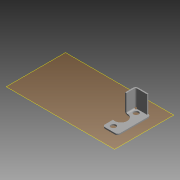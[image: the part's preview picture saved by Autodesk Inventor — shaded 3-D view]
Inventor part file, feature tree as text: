
AUTODESK INVENTOR PART (.ipt)
format: ipt  version: 2015 (Build 190159000, 159)  size: 176,640 bytes
history: native  units: mm
features: sheet_metal_op x10, sketch x4, other x4, reference x3, plane x1, hole x1
ambient origin geometry x8: Origin, YZ Plane, XZ Plane, XY Plane, X Axis, Y Axis, Z Axis, Center Point
bodies: Solid1 (feature_tree)
feature tree (23):
  plane  "Work Plane1"
  sheet_metal_op  "Face1"
  sheet_metal_op  "Flange4"
  sheet_metal_op  "Flange5"
  sheet_metal_op  "Flange6"
  hole  "Hole3"  [1 undecoded]
  sketch  "Sketch1"  dims[d0=5.0mm d2=1.0mm]
  reference  "Reference1"
  reference  "Reference2"
  reference  "Reference3"
  other  "Plate1"
  sketch  "Sketch5"  dims[d53=2.0mm]
  other  "Plate5"
  sheet_metal_op  "Bend4"
  sheet_metal_op  "Corner4"
  sketch  "Sketch6"  dims[d57=8.0mm]
  other  "Plate6"
  sheet_metal_op  "Bend5"
  sheet_metal_op  "Corner5"
  sketch  "Sketch7"  dims[d60=1.0mm d61=0.5mm d62=2.0mm d63=1.0mm d64=15.0mm d65=90.0deg d66=1.0mm d67=4.0mm d68=1.0mm d69=1.0mm d70=1.0mm d71=0.5mm d72=2.0mm d73=1.0mm d74=12.0mm d75=90.0deg d76=1.0mm d77=4.0mm d78=1.0mm d79=1.0mm d80=1.0mm d81=0.5mm d82=2.0mm d83=1.0mm d84=1.0mm d85=0.0mm d86=1.0mm d87=4.0mm d88=1.0mm d89=1.0mm d90=4.0mm d91=4.0mm d92=3.0mm d93=6.0mm d94=4.0mm d95=2.0mm d96=90.0deg d97=1.0mm d98=20.594885mm d99=4.0mm d100=135.0deg]
  other  "Plate7"
  sheet_metal_op  "Bend6"
  sheet_metal_op  "Corner6"
note: 1 required parameter value undecoded (feature->parameter linkage not recoverable at this tier; creation-order binding heuristic only, values carry confidence <= 0.55)
